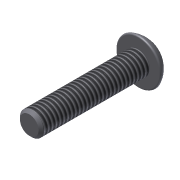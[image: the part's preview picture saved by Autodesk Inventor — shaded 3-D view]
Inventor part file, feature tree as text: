
AUTODESK INVENTOR PART (.ipt)
format: ipt  version: 2013 (Build 170138000, 138)  size: 123,904 bytes
history: native  units: in
note: dims shown in document units (in); Inventor stores cm internally (conversion verified against a paired STEP export)
features: sketch x3, extrude x2, revolve x1, chamfer x1, thread x1
ambient origin geometry x8: Origin, YZ Plane, XZ Plane, XY Plane, X Axis, Y Axis, Z Axis, Center Point
bodies: Solid1 (feature_tree)
feature tree (8):
  extrude  "Extrusion1"  Depth=0.875in TaperAngle=0.0deg
  revolve  "Revolution1"  [1 undecoded]
  extrude  "Extrusion2"  Depth=0.125in
  chamfer  "Chamfer1"  Distance=0.0625in
  thread  "Thread1"  [1 undecoded]
  sketch  "Sketch1"  dims[d0=0.19in d1=0.875in d2=0.0in]
  sketch  "Sketch2"  dims[d3=0.101in d6=0.08in]
  sketch  "Sketch3"  dims[d7=90.0deg d8=0.125in d9=0.0625in d10=0.0in d12=0.1805in d13=0.02in d14=0.125in d15=45.0deg d16=1.0in d17=0.0in]
note: 2 required parameter values undecoded (feature->parameter linkage not recoverable at this tier; creation-order binding heuristic only, values carry confidence <= 0.55)